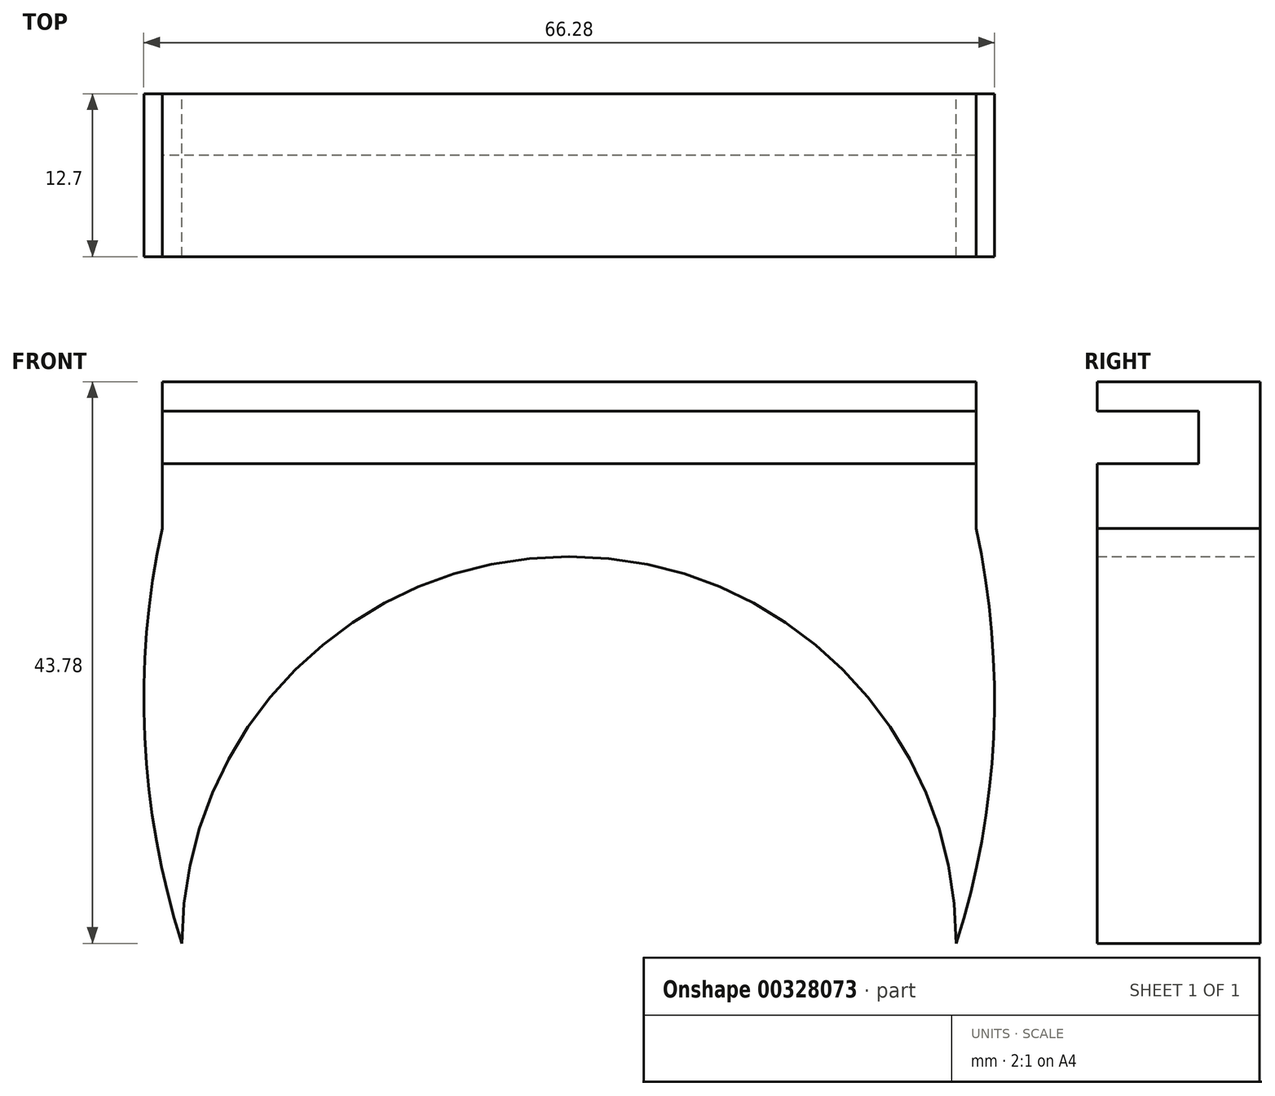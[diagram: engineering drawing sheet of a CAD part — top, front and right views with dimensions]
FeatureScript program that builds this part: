
annotation { "Feature Type Name" : "Feature", "Feature Type Description" : "" }
export const myFeature = defineFeature(function(context is Context, id is Id, definition is map)
    precondition{}
    {
        {
            var Q0;
            Q0=qCreatedBy(makeId("Front.planeOp"),FACE);
            var sketch = newSketch(context, id + "F0", { "sketchPlane" : qUnion([Q0])});
            skPoint(sketch, "E0.middle", {"position": v(0, 0) * mm});
            skArc(sketch, "E1", {"start": v(30.16, -19.05) * mm, "mid": v(0, 11.11) * mm, "end": v(-30.16, -19.05) * mm});
            skArc(sketch, "E2", {"start": v(-31.7, 13.3) * mm, "mid": v(-33.07, -2.98) * mm, "end": v(-30.16, -19.05) * mm});
            skArc(sketch, "E3.MirrorCS", {"start": v(31.7, 13.3) * mm, "mid": v(33.07, -2.98) * mm, "end": v(30.16, -19.05) * mm});
            skLineSegment(sketch, "E4", {"start": v(-31.7, 13.3) * mm, "end": v(31.7, 13.3) * mm});
            skPoint(sketch, "E0.top.end.orphan", {"position": v(-30.16, 19.05) * mm});
            skPoint(sketch, "E0.top.start.orphan", {"position": v(30.16, 19.05) * mm});
            skLineSegment(sketch, "E5.bottom", {"start": v(-31.7, 13.3) * mm, "end": v(31.71, 13.3) * mm});
            skLineSegment(sketch, "E5.top", {"start": v(-31.7, 24.73) * mm, "end": v(31.71, 24.73) * mm});
            skLineSegment(sketch, "E5.left", {"start": v(-31.7, 13.3) * mm, "end": v(-31.7, 24.73) * mm});
            skLineSegment(sketch, "E5.right", {"start": v(31.71, 13.3) * mm, "end": v(31.71, 24.73) * mm});
            skSolve(sketch);
        }
        {
            var Q0;
            Q0 = qSketchRegion(id + "F0", true);
            extrude(context, id + "F1", {"entities" : qUnion([Q0]), "depth" : 12.7 * mm});
        }
        {
            var Q0;
            Q0=makeQuery(id+"F1.opExtrude","SWEPT_FACE",FACE,{"disambiguationData":[OSD([sQuery(id+"F0.wireOp",EDGE,"E5.left")])]});
            var sketch = newSketch(context, id + "F2", { "sketchPlane" : qUnion([Q0])});
            skLineSegment(sketch, "E6.bottom", {"start": v(12.7, 22.43) * mm, "end": v(4.8, 22.43) * mm});
            skLineSegment(sketch, "E6.top", {"start": v(12.7, 18.34) * mm, "end": v(4.8, 18.34) * mm});
            skLineSegment(sketch, "E6.left", {"start": v(12.7, 22.43) * mm, "end": v(12.7, 18.34) * mm});
            skLineSegment(sketch, "E6.right", {"start": v(4.8, 22.43) * mm, "end": v(4.8, 18.34) * mm});
            skSolve(sketch);
        }
        {
            var Q0;
            Q0 = qSketchRegion(id + "F2", true);
            extrude(context, id + "F3", {"entities" : qUnion([Q0]), "operationType" : NewBodyOperationType.REMOVE, "endBound" : BoundingType.THROUGH_ALL, "oppositeDirection" : true, "depth" : 25.4 * mm});
        }
    });
